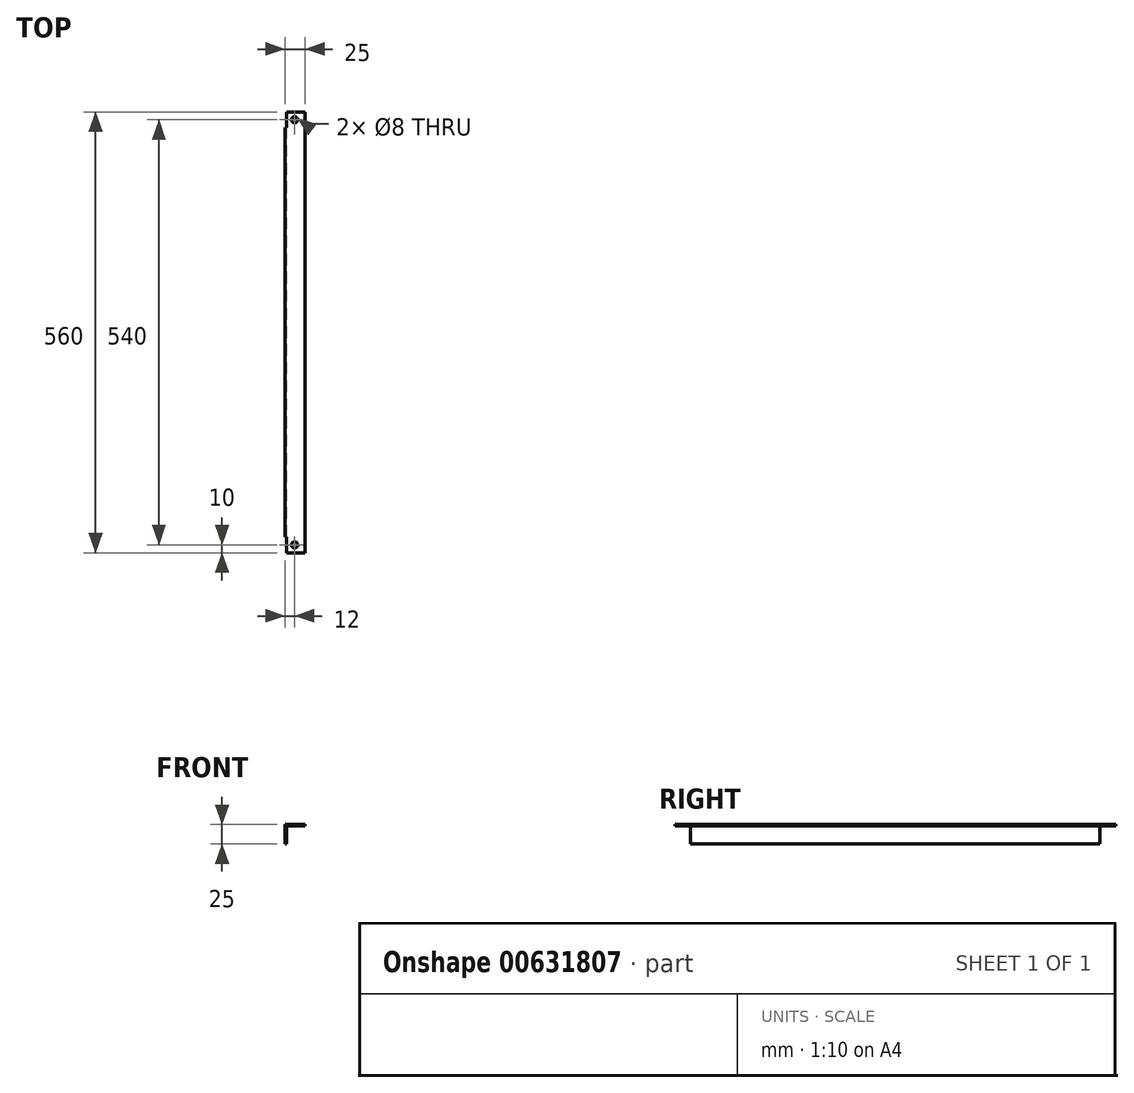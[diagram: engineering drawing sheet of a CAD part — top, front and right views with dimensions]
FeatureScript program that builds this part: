
annotation { "Feature Type Name" : "Feature", "Feature Type Description" : "" }
export const myFeature = defineFeature(function(context is Context, id is Id, definition is map)
    precondition{}
    {
        {
            var Q0;
            Q0=qCreatedBy(makeId("Front.planeOp"),FACE);
            var sketch = newSketch(context, id + "F0", { "sketchPlane" : qUnion([Q0])});
            skLineSegment(sketch, "E0", {"start": v(-1, 1) * mm, "end": v(24, 1) * mm});
            skLineSegment(sketch, "E1", {"start": v(24, 1) * mm, "end": v(24, -1) * mm});
            skLineSegment(sketch, "E2", {"start": v(24, -1) * mm, "end": v(1, -1) * mm});
            skLineSegment(sketch, "E3", {"start": v(1, -1) * mm, "end": v(1, -24) * mm});
            skLineSegment(sketch, "E4", {"start": v(1, -24) * mm, "end": v(-1, -24) * mm});
            skLineSegment(sketch, "E5", {"start": v(-1, -24) * mm, "end": v(-1, 1) * mm});
            skSolve(sketch);
        }
        {
            var Q0;
            Q0 = qSketchRegion(id + "F0", true);
            extrude(context, id + "F1", {"entities" : qUnion([Q0]), "endBound" : BoundingType.SYMMETRIC, "depth" : 560 * mm, "offsetDistance" : 25 * mm});
        }
        {
            var Q0;
            Q0=makeQuery(id+"F1.opExtrude","SWEPT_FACE",FACE,{"disambiguationData":[OSD([sQuery(id+"F0.wireOp",EDGE,"E0")])]});
            var sketch = newSketch(context, id + "F2", { "sketchPlane" : qUnion([Q0])});
            skLineSegment(sketch, "E6.bottom", {"start": v(-1, -280) * mm, "end": v(1, -280) * mm});
            skLineSegment(sketch, "E6.top", {"start": v(-1, -260) * mm, "end": v(1, -260) * mm});
            skLineSegment(sketch, "E6.left", {"start": v(-1, -280) * mm, "end": v(-1, -260) * mm});
            skLineSegment(sketch, "E6.right", {"start": v(1, -280) * mm, "end": v(1, -260) * mm});
            skLineSegment(sketch, "E7.bottom", {"start": v(-1, 280) * mm, "end": v(1, 280) * mm});
            skLineSegment(sketch, "E7.top", {"start": v(-1, 260) * mm, "end": v(1, 260) * mm});
            skLineSegment(sketch, "E7.left", {"start": v(-1, 280) * mm, "end": v(-1, 260) * mm});
            skLineSegment(sketch, "E7.right", {"start": v(1, 280) * mm, "end": v(1, 260) * mm});
            skCircle(sketch, "E8", {"center": v(11, 270) * mm, "radius": 4 * mm});
            skPoint(sketch, "E8.centerSnap0", {"position": v(1, 270) * mm});
            skCircle(sketch, "E9", {"center": v(11, -270) * mm, "radius": 4 * mm});
            skPoint(sketch, "E9.centerSnap0", {"position": v(1, -270) * mm});
            skSolve(sketch);
        }
        {
            var Q0;
            Q0 = qSketchRegion(id + "F2", true);
            extrude(context, id + "F3", {"entities" : qUnion([Q0]), "operationType" : NewBodyOperationType.REMOVE, "oppositeDirection" : true, "depth" : 42 * mm, "offsetDistance" : 25 * mm});
        }
    });
